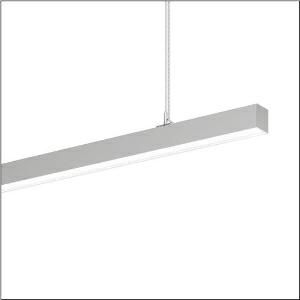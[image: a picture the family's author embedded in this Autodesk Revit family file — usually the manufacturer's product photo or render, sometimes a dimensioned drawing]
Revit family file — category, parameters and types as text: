
# Revit family: silica_r__21_51mx33da37sb_bea4
name_source: partatom
category: Lighting Fixtures
units: mm (PartAtom-declared; Revit-internal decimal feet)

## family parameters
Cut with Voids When Loaded = No
Host = Face
Light Source = No
Part Type = Normal
Room Calculation Point = No
Round Connector Dimension = Use Diameter
Shared = No

## types (1)
- --- (1 x LED, 5910 lm, 41.3 W, 3000K)
    Apparent Load = 41 VA
    CIE Flux Codes = 78 96 99 55 100
    Color Rendering = 80
    Color Temperature = 3000K
    Default Elevation = 1800 mm
    Description = Silica® 21, office luminaire, primary optical cover: prismatic diffuser, of PMMA, CAT 2 (L<= 3000cd/m²), light emission: direct/indirect distribution, primary light characteristic: symmetric, installation type: suspended mounting, LED, rated luminous flux: 5.910lm, luminous efficacy: 143lm/W, light colour: 830, colour temperature: 3000K, with terminal, 3+2-pole, max. 2.5mm², mains connection: 220..240V, AC, 50/60Hz, rated input power: 41.3W, luminaire housing, of aluminium, metallic grey (RAL 9006), length: 1.204mm, width: 53mm, height: 53mm, protection rating (complete): IP20, insulation class (complete): insulation class I (protective earthing), certification: CE, permissible operating ambient temperature: 0..+35°C, standard: EN 50419, packaging unit: 1 piece
    Height = 53 mm
    Lamp = 1 x LED
    Lamp Light Flux = 5910 lm
    Lamp Power = 41.3 W
    Lamp count = 1
    Length = 1204 mm
    Luminous efficacy = 143 lm/W
    Manufacturer = Siteco
    ModVariant = No
    Model = 51MX33DA37SB
    Mounting Place = Ceiling
    Mounting Type = Pendant
    Number of Poles = 1
    OnlyDefault = Yes
    Power Factor = 1
    Product Name = Silica® 21
    Product group = office luminaire | ceiling pendant
    ProductGroupID = 902
    Protection Class = Protection class I
    Protection Degree = IP 20
    RLX_Detail_Level = 1
    RLX_Emergency_Light_Flux = 0 lm
    RLX_Emergency_Type = 0
    RLX_Emergency_Type_DB = No
    RlxData = <blob elided: 23325 chars, md5=13036485>
    Socket = socket
    Standby Power = 0 W
    System Light Flux = 5910 lm
    System Power = 41 W
    Type Comments = factory setting: luminous flux: 100 % | dim-lin: 254 | 345 mA
    Type Image = l_1297747.jpg
    URL = http://relux.com
    VarID = @adj_048905
    Voltage = 0 V
    Weight = 0.00 kg
    Width = 53 mm

## geometry (parser evidence)
native form markers: Blend x4, Sweep x13
no freeform markers — native parametric forms only
